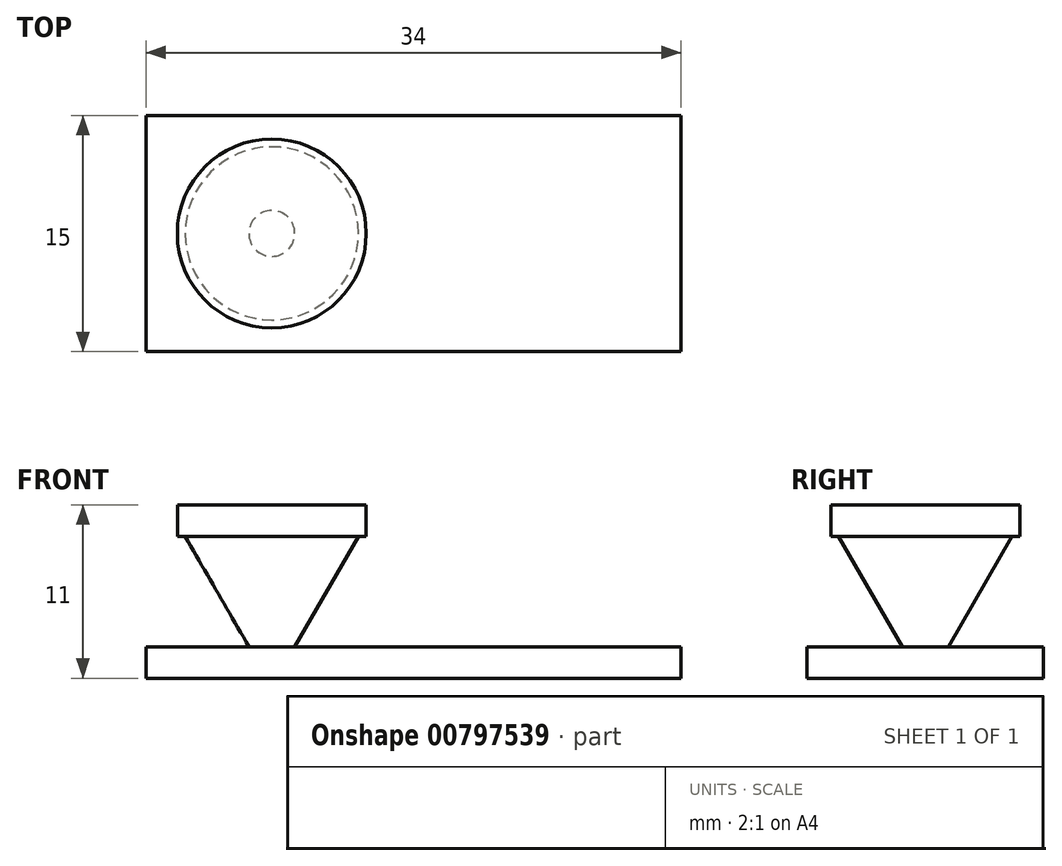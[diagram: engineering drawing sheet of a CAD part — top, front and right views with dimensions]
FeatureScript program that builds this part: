
annotation { "Feature Type Name" : "Feature", "Feature Type Description" : "" }
export const myFeature = defineFeature(function(context is Context, id is Id, definition is map)
    precondition{}
    {
        {
            var Q0;
            Q0=qCreatedBy(makeId("Front.planeOp"),FACE);
            var sketch = newSketch(context, id + "F0", { "sketchPlane" : qUnion([Q0])});
            skLineSegment(sketch, "E0.bottom", {"start": v(0, 0) * mm, "end": v(6, 0) * mm});
            skLineSegment(sketch, "E0.top", {"start": v(0, -2) * mm, "end": v(6, -2) * mm});
            skLineSegment(sketch, "E0.left", {"start": v(0, 0) * mm, "end": v(0, -2) * mm});
            skLineSegment(sketch, "E0.right", {"start": v(6, 0) * mm, "end": v(6, -2) * mm});
            skLineSegment(sketch, "E1", {"start": v(5.5, -2) * mm, "end": v(1.46, -9) * mm});
            skLineSegment(sketch, "E2", {"start": v(1.46, -9) * mm, "end": v(0, -9) * mm});
            skLineSegment(sketch, "E3", {"start": v(0, -9) * mm, "end": v(0, -2) * mm});
            skLineSegment(sketch, "E4.bottom", {"start": v(-8, -9) * mm, "end": v(26, -9) * mm});
            skLineSegment(sketch, "E4.top", {"start": v(-8, -11) * mm, "end": v(26, -11) * mm});
            skLineSegment(sketch, "E4.left", {"start": v(-8, -9) * mm, "end": v(-8, -11) * mm});
            skLineSegment(sketch, "E4.right", {"start": v(26, -9) * mm, "end": v(26, -11) * mm});
            skSolve(sketch);
        }
        {
            var Q0;
            Q0=makeQuery(id+"F0.imprint","IMPRINT",FACE,{"disambiguationData":[TD([[makeQuery(id+"F0.imprint","IMPRINT",EDGE,{"derivedFrom":sQuery(id+"F0.wireOp",EDGE,"E0.bottom")}),-1.0]])]});
            var Q1;
            {var subQ2=sQuery(id+"F0.wireOp",EDGE,"E1");Q1=makeQuery(id+"F0.imprint","IMPRINT",FACE,{"disambiguationData":[TD([[makeQuery(id+"F0.imprint","IMPRINT",EDGE,{"derivedFrom":subQ2}),-1.0]])]});}
            var Q2;
            Q2=sQuery(id+"F0.wireOp",EDGE,"E3");
            revolve(context, id + "F1", {"surfaceOperationType" : NewSurfaceOperationType.NEW, "entities" : qUnion([Q0, Q1]), "axis" : qUnion([Q2]), "revolveType" : RevolveType.FULL});
        }
        {
            var Q0;
            Q0=makeQuery(id+"F0.imprint","IMPRINT",FACE,{"disambiguationData":[TD([[makeQuery(id+"F0.imprint","IMPRINT",EDGE,{"derivedFrom":sQuery(id+"F0.wireOp",EDGE,"E4.top")}),1.0]])]});
            extrude(context, id + "F2", {"entities" : qUnion([Q0]), "operationType" : NewBodyOperationType.ADD, "endBound" : BoundingType.SYMMETRIC, "depth" : 15 * mm, "offsetDistance" : 25 * mm});
        }
    });
